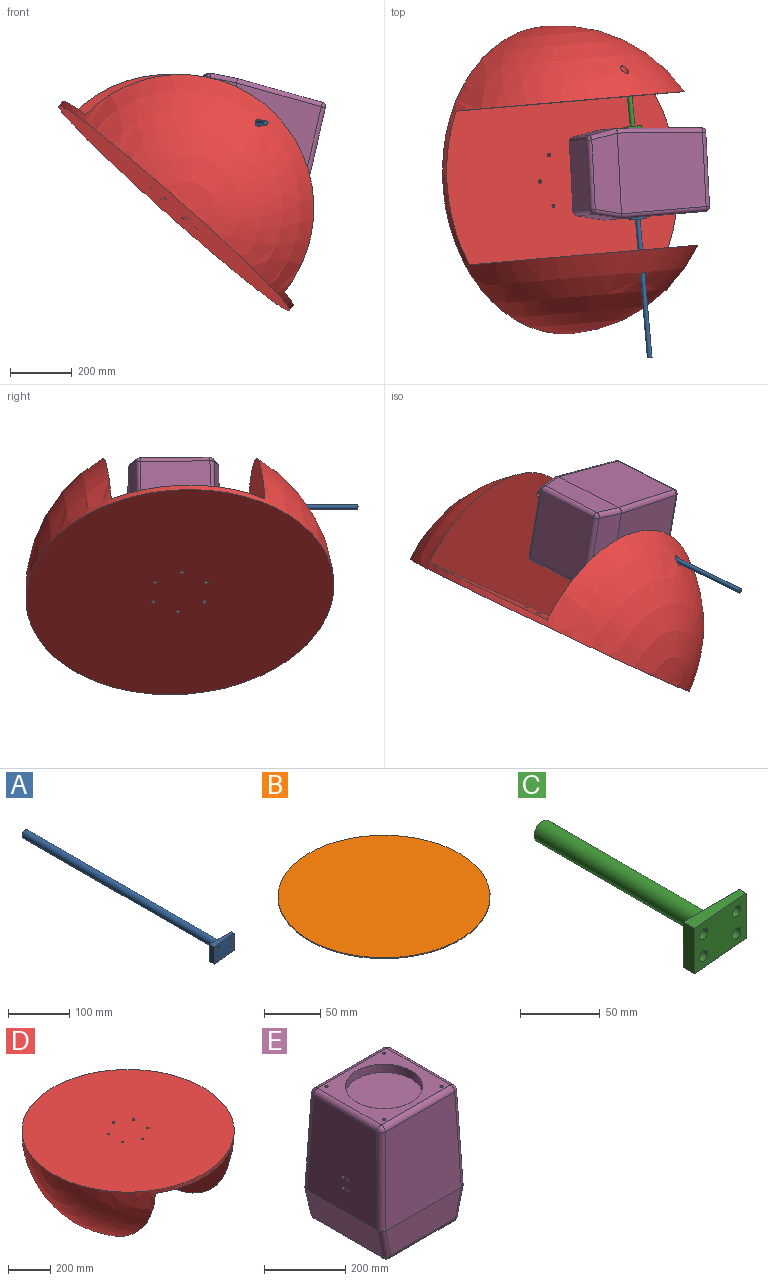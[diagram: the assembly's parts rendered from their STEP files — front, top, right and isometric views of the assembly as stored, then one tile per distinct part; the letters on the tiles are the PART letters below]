
ASSEMBLY  parts=5 mates=4
PART A: 12 faces, bbox 50.1x460.5x35.1 mm
  f0: plane 35x6mm, normal (1,0,0), area 210mm2, adj f1,f3,f4,f5
  f1: plane 50x35mm, normal (0,1,0), area 1372.2mm2, adj f0,f2,f4,f5,f6,f7,f8,f9
  f2: plane 35x10.33mm, normal (-1,0,0), area 361.6mm2, adj f1,f3,f4,f5
  f3: plane 50.15x35.15mm, normal (0.09,-1,0), area 1554.7mm2, adj f0,f2,f4,f5,f6,f7,f8,f9
  f4: plane 50x10.33mm, normal (0,0,1), area 408.2mm2, adj f0,f1,f2,f3
  f5: plane 50x10.33mm, normal (0,0,-1), area 408.2mm2, adj f0,f1,f2,f3
  f6: cylinder r=4mm len=9.9mm, axis (0,1,0), area 240mm2, adj f1,f3
  f7: cylinder r=4mm len=8mm, axis (0,1,0), area 170.4mm2, adj f1,f3
  f8: cylinder r=4mm len=8mm, axis (0,1,0), area 170.4mm2, adj f1,f3
  f9: cylinder r=4mm len=9.9mm, axis (0,1,0), area 240mm2, adj f1,f3
  f10: cylinder r=7.5mm len=450mm, axis (0,-1,0), area 21205.8mm2, adj f1,f11
  f11: plane 15x15mm, normal (0,1,0), area 176.7mm2, adj f10
PART B: 3 faces, bbox 189x189x1 mm
  f0: cylinder r=94.5mm len=189mm, axis (0,0,1), area 593.8mm2, adj f1,f2
  f1: plane 189x189mm, normal (0,0,-1), area 28055.2mm2, adj f0
  f2: plane 189x189mm, normal (0,0,1), area 28055.2mm2, adj f0
PART C: 12 faces, bbox 50.1x160.5x35.1 mm
  f0: plane 35x6mm, normal (1,0,0), area 210mm2, adj f1,f3,f4,f5
  f1: plane 50x35mm, normal (0,1,0), area 1372.2mm2, adj f0,f2,f4,f5,f6,f7,f8,f9
  f2: plane 35x10.33mm, normal (-1,0,0), area 361.6mm2, adj f1,f3,f4,f5
  f3: plane 50.15x35.15mm, normal (0.09,-1,0), area 1554.7mm2, adj f0,f2,f4,f5,f6,f7,f8,f9
  f4: plane 50x10.33mm, normal (0,0,1), area 408.2mm2, adj f0,f1,f2,f3
  f5: plane 50x10.33mm, normal (0,0,-1), area 408.2mm2, adj f0,f1,f2,f3
  f6: cylinder r=4mm len=9.9mm, axis (0,1,0), area 240mm2, adj f1,f3
  f7: cylinder r=4mm len=8mm, axis (0,1,0), area 170.4mm2, adj f1,f3
  f8: cylinder r=4mm len=8mm, axis (0,1,0), area 170.4mm2, adj f1,f3
  f9: cylinder r=4mm len=9.9mm, axis (0,1,0), area 240mm2, adj f1,f3
  f10: cylinder r=7.5mm len=150mm, axis (0,-1,0), area 7068.6mm2, adj f1,f11
  f11: plane 15x15mm, normal (0,1,0), area 176.7mm2, adj f10
PART D: 13 faces, bbox 1000x1000x500 mm
  f0: sphere r=500mm, area 804878.2mm2, adj f1,f2,f3,f4,f5,f6
  f1: plane 1000x1000mm, normal (0,0,1), area 784719.6mm2, adj f0,f7,f8,f9,f10,f11,f12
  f2: plane 865.1x413.01mm, normal (1,0,0), area 276719.1mm2, adj f0,f4,f6
  f3: plane 865.1x413.01mm, normal (-1,0,0), area 276719.1mm2, adj f0,f4,f5
  f4: plane 999.2x500mm, normal (0,0,-1), area 477208.1mm2, adj f0,f2,f3,f7,f8,f9,f10,f11
  f5: cylinder r=12.5mm len=99.56mm, axis (-1,0,0), area 6748.9mm2, adj f0,f3
  f6: cylinder r=12.5mm len=99.56mm, axis (-1,0,0), area 6749.2mm2, adj f0,f2
  f7: cylinder r=6mm len=20mm, axis (0,0,-1), area 754mm2, adj f1,f4
  f8: cylinder r=6mm len=20mm, axis (0,0,-1), area 754mm2, adj f1,f4
  f9: cylinder r=6mm len=20mm, axis (0,0,-1), area 754mm2, adj f1,f4
  f10: cylinder r=6mm len=20mm, axis (0,0,-1), area 754mm2, adj f1,f4
  f11: cylinder r=6mm len=20mm, axis (0,0,-1), area 754mm2, adj f1,f4
  f12: cylinder r=6mm len=20mm, axis (0,0,-1), area 754mm2, adj f1,f4
PART E: 48 faces, bbox 292.1x276.2x400.1 mm
  f0: plane 241.08x221.27mm, normal (0,0,1), area 24790.2mm2, adj f10,f12,f15,f18,f19,f36,f38,f40
  f1: plane 285.66x262.04mm, normal (0,1,0.04), area 71923.6mm2, adj f8,f15,f16,f21,f25,f29
  f2: plane 285.55x246.02mm, normal (1,0,0.04), area 66561.1mm2, adj f9,f19,f25,f28,f44,f45,f46,f47
  f3: plane 285.66x262.04mm, normal (0,-1,0.04), area 71923.6mm2, adj f6,f17,f18,f23,f28,f32
  f4: plane 285.61x246.08mm, normal (-1,0,0.04), area 66561.1mm2, adj f7,f12,f16,f17,f44,f45,f46,f47
  f5: plane 240.89x225.65mm, normal (0,0,-1), area 54355mm2, adj f22,f30,f31,f35
  f6: plane 261.53x85.45mm, normal (0,-1,-0.03), area 20824.1mm2, adj f3,f23,f31,f32
  f7: plane 246.17x88.08mm, normal (-0.98,0,-0.21), area 21918.6mm2, adj f4,f16,f17,f21,f22,f23
  f8: plane 261.53x85.45mm, normal (0,1,-0.03), area 20824.1mm2, adj f1,f21,f29,f30
  f9: plane 246.17x88.08mm, normal (0.98,0,-0.21), area 21918.6mm2, adj f2,f25,f28,f29,f32,f35
  f10: cylinder r=95mm len=190mm, axis (0,0,1), area 14922.6mm2, adj f0,f11
  f11: plane 190x190mm, normal (0,0,1), area 28352.9mm2, adj f10
  f12: cylinder r=15mm len=221.27mm, axis (0,-1,0), area 5091.9mm2, adj f0,f4,f13,f14
  f13: sphere r=15mm, area 335.5mm2, adj f12,f15,f16
  f14: sphere r=15mm, area 335.5mm2, adj f12,f17,f18
  f15: cylinder r=15mm len=241.08mm, axis (1,0,0), area 5523.7mm2, adj f0,f1,f13,f20
  f16: cylinder r=15mm len=286.08mm, axis (0.04,-0.04,1), area 6734.2mm2, adj f1,f4,f7,f13,f21
  f17: cylinder r=15mm len=286.08mm, axis (-0.04,-0.04,-1), area 6734.2mm2, adj f3,f4,f7,f14,f23
  f18: cylinder r=15mm len=241.08mm, axis (1,0,0), area 5523.7mm2, adj f0,f3,f14,f24
  f19: cylinder r=15mm len=221.27mm, axis (0,-1,0), area 5091.9mm2, adj f0,f2,f20,f24
  f20: sphere r=15mm, area 335.5mm2, adj f15,f19,f25
  f21: cylinder r=15mm len=90.75mm, axis (-0.21,0.03,0.98), area 2096.1mm2, adj f1,f7,f8,f16,f26
  f22: cylinder r=15mm len=240.89mm, axis (0,-1,0), area 4927.8mm2, adj f5,f7,f26,f27
  f23: cylinder r=15mm len=90.75mm, axis (0.21,0.03,-0.98), area 2096.1mm2, adj f3,f6,f7,f17,f27
  f24: sphere r=15mm, area 335.5mm2, adj f18,f19,f28
  f25: cylinder r=15mm len=286.08mm, axis (0.04,0.04,-1), area 6734.2mm2, adj f1,f2,f9,f20,f29
  f26: sphere r=15mm, area 300.3mm2, adj f21,f22,f30
  f27: sphere r=15mm, area 300.3mm2, adj f22,f23,f31
  f28: cylinder r=15mm len=286.08mm, axis (-0.04,0.04,1), area 6734.2mm2, adj f2,f3,f9,f24,f32
  f29: cylinder r=15mm len=90.75mm, axis (-0.21,-0.03,-0.98), area 2096.1mm2, adj f1,f8,f9,f25,f33
  f30: cylinder r=15mm len=225.65mm, axis (1,0,0), area 5215.1mm2, adj f5,f8,f26,f33
  f31: cylinder r=15mm len=225.65mm, axis (1,0,0), area 5215.1mm2, adj f5,f6,f27,f34
  f32: cylinder r=15mm len=90.75mm, axis (0.21,-0.03,0.98), area 2096.1mm2, adj f3,f6,f9,f28,f34
  f33: sphere r=15mm, area 300.3mm2, adj f29,f30,f35
  f34: sphere r=15mm, area 300.3mm2, adj f31,f32,f35
  f35: cylinder r=15mm len=240.89mm, axis (0,-1,0), area 4927.8mm2, adj f5,f9,f33,f34
  f36: cylinder r=4mm len=10mm, axis (0,0,1), area 251.3mm2, adj f0,f37
  f37: plane 8x8mm, normal (0,0,1), area 50.3mm2, adj f36
  f38: cylinder r=4mm len=10mm, axis (0,0,1), area 251.3mm2, adj f0,f39
  f39: plane 8x8mm, normal (0,0,1), area 50.3mm2, adj f38
  f40: cylinder r=4mm len=10mm, axis (0,0,1), area 251.3mm2, adj f0,f41
  f41: plane 8x8mm, normal (0,0,1), area 50.3mm2, adj f40
  f42: cylinder r=4mm len=10mm, axis (0,0,1), area 251.3mm2, adj f0,f43
  f43: plane 8x8mm, normal (0,0,1), area 50.3mm2, adj f42
  f44: cylinder r=4mm len=287.4mm, axis (-1,0,0), area 7215.6mm2, adj f2,f4
  f45: cylinder r=4mm len=285.1mm, axis (-1,0,0), area 7158mm2, adj f2,f4
  f46: cylinder r=4mm len=285.05mm, axis (-1,0,0), area 7156.7mm2, adj f2,f4
  f47: cylinder r=4mm len=287.45mm, axis (-1,0,0), area 7216.9mm2, adj f2,f4
PLACE A rot(axis=(-0.11,0,-0.99),175.1deg) t=(858,76.85,373.08)mm
PLACE B rot(axis=(0.02,-1,0.04),76.9deg) t=(1307.76,243.98,273.1)mm
PLACE C rot(axis=(0.05,-1,0),166.9deg) t=(850.32,368.05,404.94)mm
PLACE D rot(axis=(0.71,-0.65,-0.25),149.6deg) t=(604.48,200.27,113.65)mm fixed
PLACE E rot(axis=(-0.64,0.6,-0.48),126.7deg) t=(771.76,217.83,398.08)mm
MATE fastened E.f4 <-> C.f3  axis (-0.01,1,-0.02) through (829.1,364.38,383.24)mm
MATE fastened A.f8 <-> E.f2  axis (0.09,-1,0) through (848.18,78.01,402.03)mm
MATE fastened E.f10 <-> B.f0  axis (0.97,0.05,-0.23) through (1039.28,230.88,335.7)mm
MATE revolute D.f5 <-> A.f10  axis (-0.09,1,0) through (871.03,-27.58,390.12)mm
